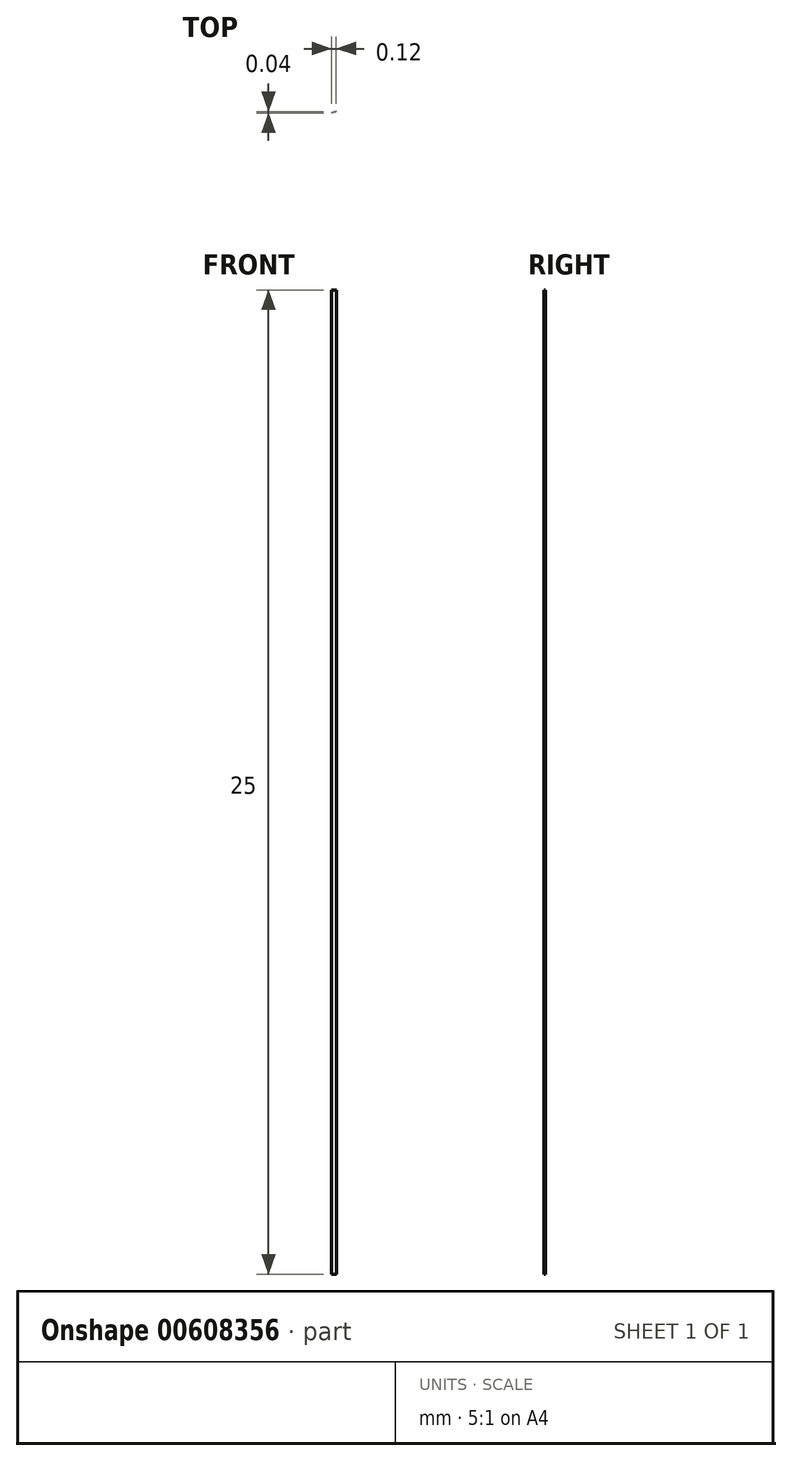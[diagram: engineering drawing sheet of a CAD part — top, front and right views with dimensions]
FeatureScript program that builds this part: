
annotation { "Feature Type Name" : "Feature", "Feature Type Description" : "" }
export const myFeature = defineFeature(function(context is Context, id is Id, definition is map)
    precondition{}
    {
        {
            var Q0;
            Q0=qCreatedBy(makeId("Top.planeOp"),FACE);
            var sketch = newSketch(context, id + "F0", { "sketchPlane" : qUnion([Q0])});
            skArc(sketch, "E0", {"start": v(-165.18, 19.32) * mm, "mid": v(-179.3, -5.24) * mm, "end": v(-154.7, -19.28) * mm});
            skArc(sketch, "E1", {"start": v(-5.82, 21.13) * mm, "mid": v(0, 20.37) * mm, "end": v(5.82, 21.13) * mm});
            skArc(sketch, "E2.MirrorC", {"start": v(165.18, 19.32) * mm, "mid": v(179.3, -5.24) * mm, "end": v(154.7, -19.28) * mm});
            skLineSegment(sketch, "E3", {"start": v(-160, 0) * mm, "end": v(0, 42.87) * mm, "construction": true});
            skLineSegment(sketch, "E4", {"start": v(0, 42.87) * mm, "end": v(160, 0) * mm, "construction": true});
            skCircle(sketch, "E5", {"center": v(0, 42.87) * mm, "radius": 5 * mm});
            skCircle(sketch, "E6", {"center": v(-160, 0) * mm, "radius": 4 * mm});
            skCircle(sketch, "E7", {"center": v(160, 0) * mm, "radius": 4 * mm});
            skLineSegment(sketch, "E8", {"start": v(-160, 0) * mm, "end": v(-154.82, -19.32) * mm, "construction": true});
            skLineSegment(sketch, "E9", {"start": v(-160, 0) * mm, "end": v(-165.18, 19.32) * mm, "construction": true});
            skLineSegment(sketch, "E10", {"start": v(0, 42.87) * mm, "end": v(-5.82, 64.6) * mm, "construction": true});
            skLineSegment(sketch, "E11", {"start": v(0, 42.87) * mm, "end": v(5.82, 21.13) * mm, "construction": true});
            skLineSegment(sketch, "E12", {"start": v(0, 42.87) * mm, "end": v(5.82, 64.6) * mm, "construction": true});
            skLineSegment(sketch, "E13", {"start": v(5.82, 64.6) * mm, "end": v(-5.82, 21.13) * mm, "construction": true});
            skLineSegment(sketch, "E14", {"start": v(160, 0) * mm, "end": v(165.18, 19.32) * mm, "construction": true});
            skLineSegment(sketch, "E15", {"start": v(160, 0) * mm, "end": v(154.82, -19.32) * mm, "construction": true});
            skLineSegment(sketch, "E16", {"start": v(5.82, 21.13) * mm, "end": v(154.82, -19.32) * mm});
            skLineSegment(sketch, "E17", {"start": v(5.82, 64.6) * mm, "end": v(165.18, 19.32) * mm});
            skLineSegment(sketch, "E18", {"start": v(-5.82, 21.13) * mm, "end": v(-154.82, -19.32) * mm});
            skLineSegment(sketch, "E19", {"start": v(-165.18, 19.32) * mm, "end": v(-5.82, 64.6) * mm});
            skArc(sketch, "E20.trimOffspring", {"start": v(6.48, 64.42) * mm, "mid": v(0, 65.38) * mm, "end": v(-6.48, 64.42) * mm});
            skSolve(sketch);
        }
        {
            var Q0;
            {var subQ1=sQuery(id+"F0.wireOp",EDGE,"E0");Q0=makeQuery(id+"F0.imprint","IMPRINT",FACE,{"disambiguationData":[TD([[makeQuery(id+"F0.imprint","IMPRINT",EDGE,{"derivedFrom":subQ1}),1.0]])]});}
            extrude(context, id + "F1", {"entities" : qUnion([Q0]), "depth" : 25 * mm, "offsetDistance" : 25 * mm});
        }
    });
